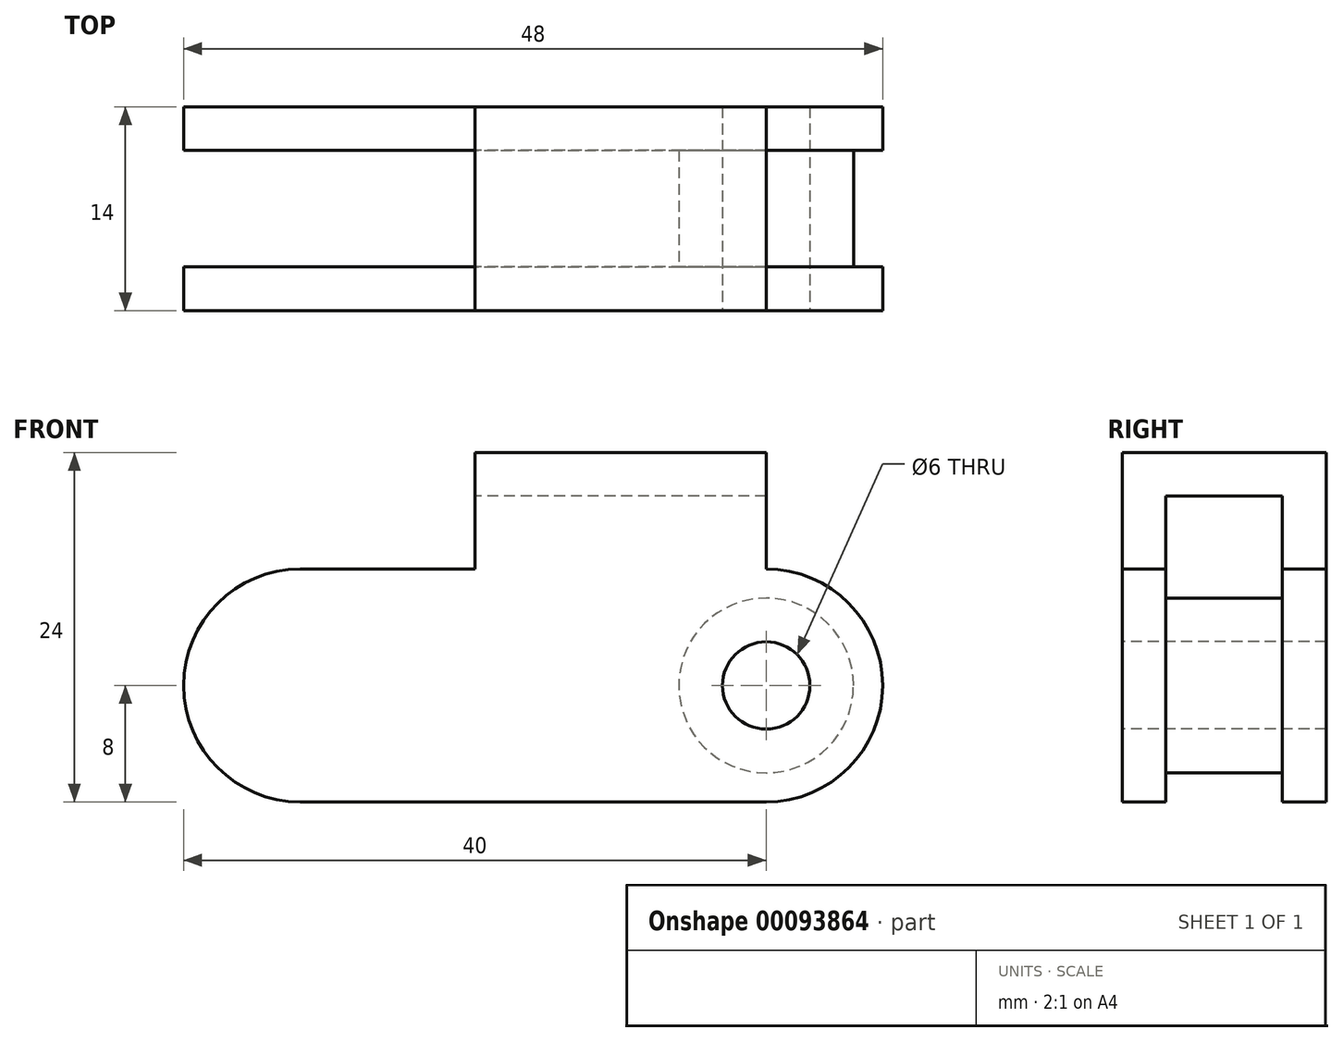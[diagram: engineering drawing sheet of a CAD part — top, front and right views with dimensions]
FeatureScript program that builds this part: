
annotation { "Feature Type Name" : "Feature", "Feature Type Description" : "" }
export const myFeature = defineFeature(function(context is Context, id is Id, definition is map)
    precondition{}
    {
        {
            var Q0;
            Q0=qCreatedBy(makeId("Front.planeOp"),FACE);
            var sketch = newSketch(context, id + "F0", { "sketchPlane" : qUnion([Q0])});
            skLineSegment(sketch, "E0", {"start": v(-16, 0) * mm, "end": v(16, 0) * mm, "construction": true});
            skCircle(sketch, "E1", {"center": v(-16, 0) * mm, "radius": 3 * mm});
            skCircle(sketch, "E2.MirrorC", {"center": v(16, 0) * mm, "radius": 3 * mm});
            skLineSegment(sketch, "E3", {"start": v(16, 0) * mm, "end": v(16, 16) * mm, "construction": true});
            skLineSegment(sketch, "E4", {"start": v(16, 16) * mm, "end": v(-4, 16) * mm, "construction": true});
            skArc(sketch, "E5.0.startCap", {"start": v(-16, -8) * mm, "mid": v(-24, 0) * mm, "end": v(-16, 8) * mm});
            skArc(sketch, "E5.0.endCap", {"start": v(16, 8) * mm, "mid": v(24, 0) * mm, "end": v(16, -8) * mm});
            skLineSegment(sketch, "E5.0.left", {"start": v(-16, 8) * mm, "end": v(-4, 8) * mm});
            skLineSegment(sketch, "E5.0.right", {"start": v(-16, -8) * mm, "end": v(16, -8) * mm});
            skLineSegment(sketch, "E6", {"start": v(16, 8) * mm, "end": v(16, 16) * mm});
            skLineSegment(sketch, "E7", {"start": v(16, 16) * mm, "end": v(-4, 16) * mm});
            skLineSegment(sketch, "E8", {"start": v(-4, 16) * mm, "end": v(-4, 8) * mm});
            skSolve(sketch);
        }
        {
            var Q0;
            Q0=makeQuery(id+"F0.imprint","IMPRINT",FACE,{"disambiguationData":[TD([[makeQuery(id+"F0.imprint","IMPRINT",EDGE,{"derivedFrom":sQuery(id+"F0.wireOp",EDGE,"E1")}),-1.0]])]});
            var Q1;
            Q1=makeQuery(id+"F0.imprint","IMPRINT",FACE,{"disambiguationData":[TD([[makeQuery(id+"F0.imprint","IMPRINT",EDGE,{"derivedFrom":sQuery(id+"F0.wireOp",EDGE,"E1")}),1.0]])]});
            var Q2;
            Q2=makeQuery(id+"F0.imprint","IMPRINT",FACE,{"disambiguationData":[TD([[makeQuery(id+"F0.imprint","IMPRINT",EDGE,{"derivedFrom":sQuery(id+"F0.wireOp",EDGE,"E2.MirrorC")}),-1.0]])]});
            extrude(context, id + "F1", {"entities" : qUnion([Q0, Q1, Q2]), "oppositeDirection" : true, "depth" : 14 * mm});
        }
        {
            var Q0;
            Q0=makeQuery(id+"F1.opExtrude","SWEPT_FACE",FACE,{"disambiguationData":[OSD([sQuery(id+"F0.wireOp",EDGE,"E5.0.left")])]});
            var Q1;
            Q1=makeQuery(id+"F1.opExtrude","SWEPT_FACE",FACE,{"disambiguationData":[OSD([sQuery(id+"F0.wireOp",EDGE,"E8")])]});
            var Q2;
            Q2=makeQuery(id+"F1.opExtrude","SWEPT_FACE",FACE,{"disambiguationData":[OSD([sQuery(id+"F0.wireOp",EDGE,"E5.0.endCap")])]});
            var Q3;
            Q3=makeQuery(id+"F1.opExtrude","SWEPT_FACE",FACE,{"disambiguationData":[OSD([sQuery(id+"F0.wireOp",EDGE,"E5.0.startCap")])]});
            var Q4;
            Q4=makeQuery(id+"F1.opExtrude","SWEPT_FACE",FACE,{"disambiguationData":[OSD([sQuery(id+"F0.wireOp",EDGE,"E5.0.right")])]});
            var Q5;
            Q5=makeQuery(id+"F1.opExtrude","SWEPT_FACE",FACE,{"disambiguationData":[OSD([sQuery(id+"F0.wireOp",EDGE,"E6")])]});
            var Q6;
            Q6=makeQuery(id+"F1.opExtrude","SWEPT_BODY",BODY,{"disambiguationData":[OSD([sQuery(id+"F0.wireOp",EDGE,"E1"),sQuery(id+"F0.wireOp",EDGE,"E2.MirrorC"),sQuery(id+"F0.wireOp",EDGE,"E5.0.startCap"),sQuery(id+"F0.wireOp",EDGE,"E5.0.endCap"),sQuery(id+"F0.wireOp",EDGE,"E5.0.left"),sQuery(id+"F0.wireOp",EDGE,"E5.0.right"),sQuery(id+"F0.wireOp",EDGE,"E6"),sQuery(id+"F0.wireOp",EDGE,"E7"),sQuery(id+"F0.wireOp",EDGE,"E8")])]});
            shell(context, id + "F2", {"entities" : qUnion([Q0, Q1, Q2, Q3, Q4, Q5]), "parts" : qUnion([Q6]), "thickness" : 3 * mm});
        }
    });
